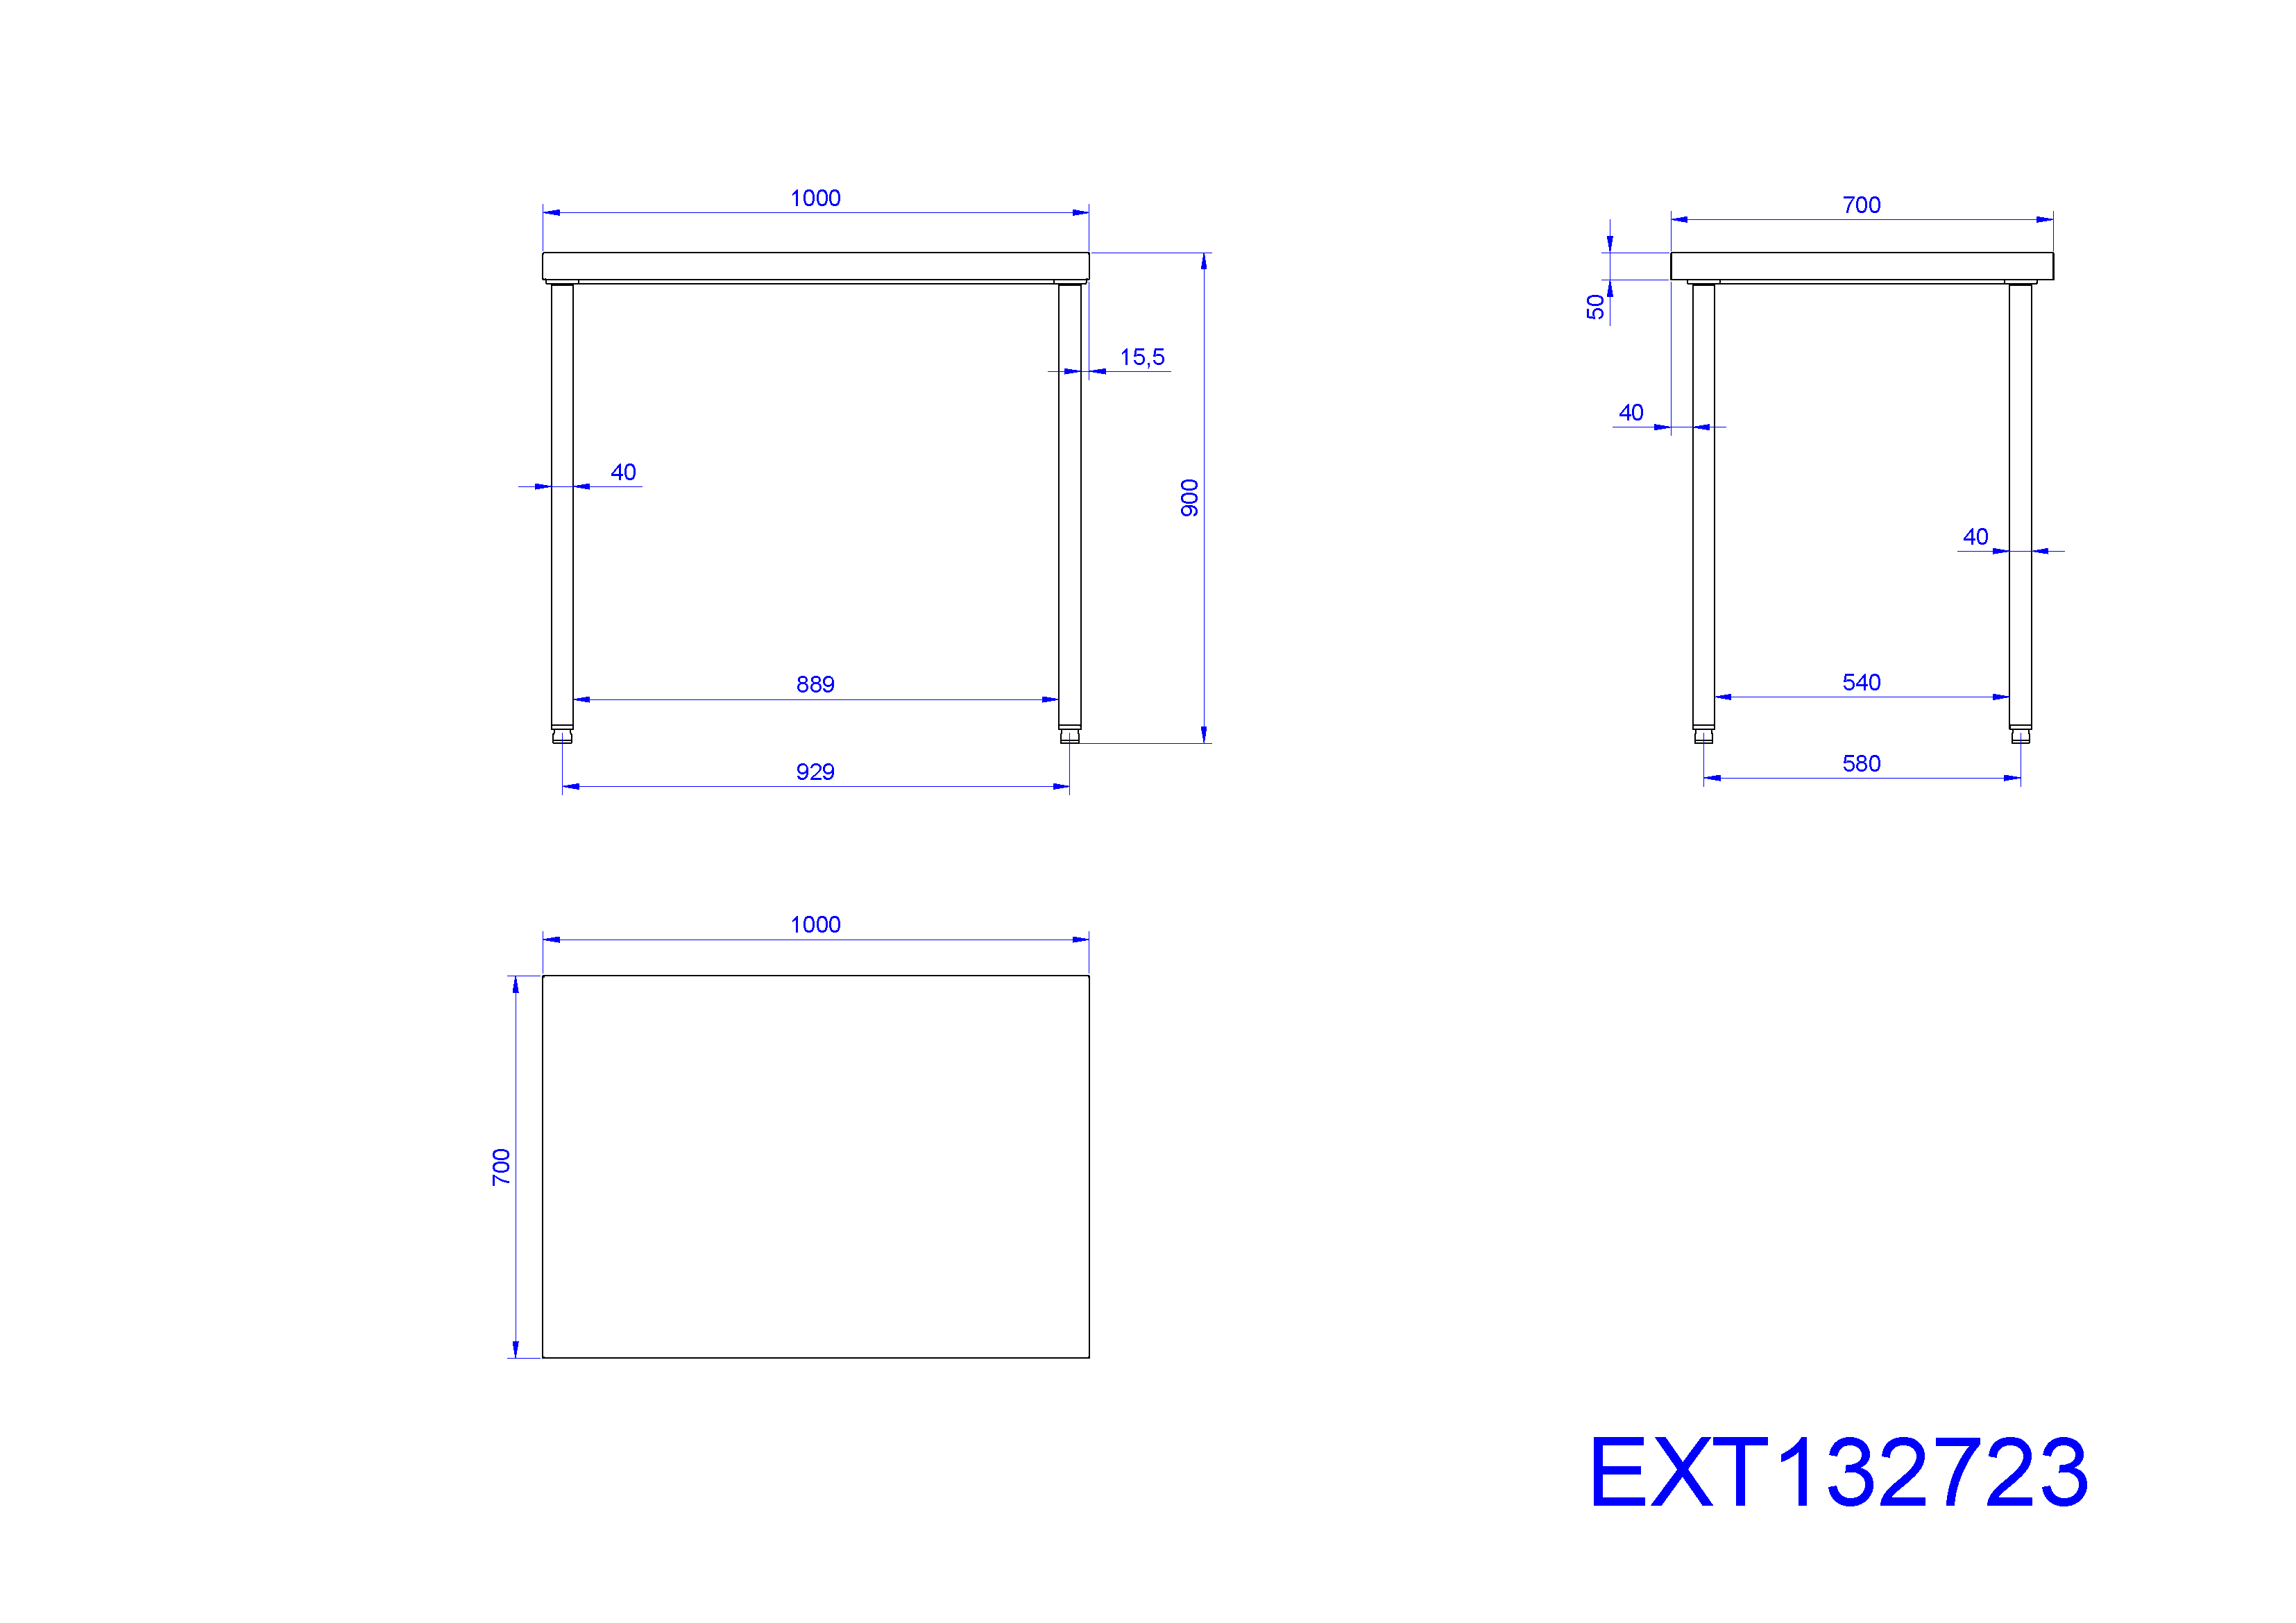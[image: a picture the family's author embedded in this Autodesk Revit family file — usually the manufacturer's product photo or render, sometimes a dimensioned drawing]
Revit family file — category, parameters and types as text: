
# Revit family: QF_ELECTROLUXPROFESSIONAL_132728_TG2000PN
name_source: partatom
category: Attrezzature speciali
units: mm (PartAtom-declared; Revit-internal decimal feet)

## family parameters
Basato su piano di lavoro = No
Condiviso = No
Punto di calcolo locali = No
Quota connettore circolare = Usa diametro
Sempre verticale = Sì
Taglio con vuoti quando caricato = No
Tipo di parte = Normale

## types (1)
- Standard
    Accessory = Sì
    Cold Water Size = 0 mm
    Compressed Air Pressure = 0.0 Pa
    Compressed Air Size = 0 mm
    Compressed Air Volume = 0.0 L/s
    Condensate Return Size = 0 mm
    Cycle = 0 Hz
    Depth Actual = 700 mm  [stored 2.29659 ft]
    Descrizione = WORK TABLE 2000 MM
    Direct Waste Size = 0 mm
    Gas Input Pressure = 0
    Gas KW = 0
    Gas Size = 0 mm
    HP = 0 HP
    Height Actual = 900 mm  [stored 2.95276 ft]
    Hot Water Size = 0 mm
    Item Number = 132728
    Length Actual = 2000 mm  [stored 6.56168 ft]
    Modello = TG2000PN
    Phase = 0
    Produttore = Electrolux Professional
    Prospetto di default = 0 mm  [stored 0 ft]
    Refrigerant Compressor Remote = Sì
    Refrigeration Liquid Line Size = 0 mm  [stored 0 ft]
    Refrigeration Suction Line Size = 0 mm  [stored 0 ft]
    Steam Consumption per Hour = 0
    Steam Supply Maximum Pressure = 0.0 Pa
    Steam Supply Minimum Pressure = 0.0 Pa
    Steam Supply Size = 0 mm
    URL = https://www.electroluxprofessional.com
    URL Manufacturer = https://www.electroluxprofessional.com
    Volts = 0 V
    Watts = 0 W
    Weight = 58.00 kg

note: source unit labels omitted for Gas Input Pressure — the stored unit's dimension contradicts the parameter name (converter mislabeling)

note: [stored X ft] marks values corroborated as IEEE doubles in the binary element streams (Revit-internal decimal feet)

## geometry (parser evidence)
native form markers: Sweep x2
no freeform markers — native parametric forms only
